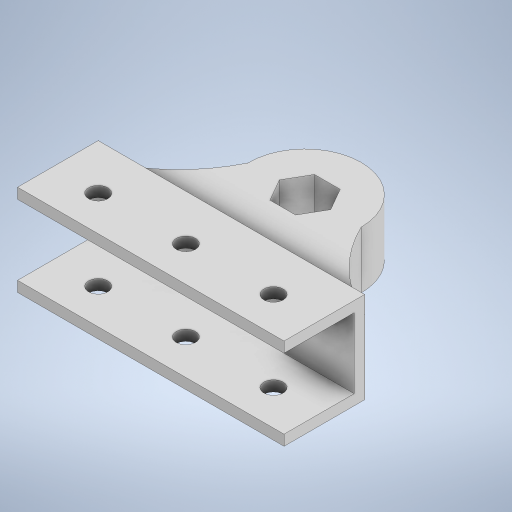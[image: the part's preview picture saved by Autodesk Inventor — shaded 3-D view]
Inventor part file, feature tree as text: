
AUTODESK INVENTOR PART (.ipt)
format: ipt  version: 2023.1 (Build 271208000, 208)  size: 310,272 bytes
history: native  units: in
note: dims shown in document units (in); Inventor stores cm internally (conversion verified against a paired STEP export)
features: sketch x7, extrude x6, hole x1
ambient origin geometry x8: Origin, YZ Plane, XZ Plane, XY Plane, X Axis, Y Axis, Z Axis, Center Point
bodies: Solid1 (feature_tree)
feature tree (14):
  extrude  "Extrusion1"  Depth=2.9921in
  extrude  "Extrusion2"  Depth=0.1181in
  extrude  "Extrusion3"  Depth=0.7874in TaperAngle=0.0deg
  sketch  "Sketch5"  dims[d8=1.2598in d10=0.1181in]
  sketch  "Sketch7"  dims[d11=0.0in d12=0.0in d13=1.2598in d14=0.1181in]
  extrude  "Extrusion4"  Depth=0.1181in
  extrude  "Extrusion5"  Depth=0.1181in
  extrude  "Extrusion6"  Depth=0.1919in TaperAngle=0.0deg
  hole  "Hole1"  [1 undecoded]
  sketch  "Sketch1"  dims[d0=2.3622in d1=2.9921in]
  sketch  "Sketch2"  dims[d2=1.0236in d3=0.0in d4=0.1181in]
  sketch  "Sketch3"  dims[d5=0.1181in d6=0.7874in d7=0.0in]
  sketch  "Sketch9"  dims[d15=0.1919in d16=0.0in d17=0.1919in d18=0.0in]
  sketch  "Sketch10"  dims[d19=0.5in d20=0.0in d21=0.0in d23=0.3937in d24=0.3937in d25=0.3937in d27=0.0in d28=0.9843in d29=0.9843in d30=0.2165in d31=0.2953in d32=0.4094in d33=0.0984in d34=90.0deg d35=0.3937in d36=0.8108in]
note: 1 required parameter value undecoded (feature->parameter linkage not recoverable at this tier; creation-order binding heuristic only, values carry confidence <= 0.55)
